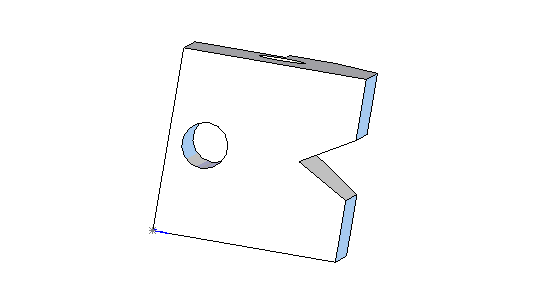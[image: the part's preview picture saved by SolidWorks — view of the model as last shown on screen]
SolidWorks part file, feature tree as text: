
SOLIDWORKS PART (.sldprt)
format: sldprt  version: not decoded by parser v0  size: 79,872 bytes
history: native  units: mm
features: sketch x4, cut_extrude x3, extrude x1 (+11 scaffold rows collapsed)
feature tree (19):
  scaffold x11  (default folders/planes/origin — collapsed)
  sketch  "Sketch1"  dims[D1=25.4mm D2=25.4mm D3=~7.536023mm]
  extrude  "Extrude1"  Depth=25.4mm
  sketch  "Sketch2"  dims[D1=6.35mm D2=3.175mm D3=~1.961917mm D4=~16.117758mm D5=~11.209871mm D6=12.7mm D7=12.7mm D8=~15.527932mm D9=~8.319067mm D10=~2.827932mm D11=~1.961917mm]
  cut_extrude  "Cut-Extrude1"  [1 undecoded]
  sketch  "Sketch3"  dims[D3=6.35mm D1=12.7mm D2=5.08mm]
  cut_extrude  "Cut-Extrude2"  [1 undecoded]
  sketch  "Sketch4"  dims[c1.D1=12.7mm c1.D2=~10.680937mm c1.D3=25.4mm c2.D2=12.7mm c2.D3=12.7mm c2.D4=~18.181497mm c2.D5=~12.736038mm]
  cut_extrude  "Cut-Extrude3"  [1 undecoded]
decode coverage: 5 of 8 modeling features carry decoded parameters
note: ~ marks probable driven/reference dimensions
note: 3 parameter values undecoded
summary: no parameter record found for 3 features
note: suppression state not decoded; provenance and decode notes live in map.json
